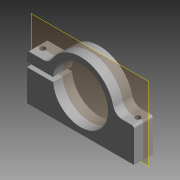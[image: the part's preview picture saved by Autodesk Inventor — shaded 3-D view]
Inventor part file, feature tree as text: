
AUTODESK INVENTOR PART (.ipt)
format: ipt  version: 2013 (Build 170138000, 138)  size: 109,568 bytes
history: native  units: in
note: dims shown in document units (in); Inventor stores cm internally (conversion verified against a paired STEP export)
features: other x3, plane x1
ambient origin geometry x8: Origin, YZ Plane, XZ Plane, XY Plane, X Axis, Y Axis, Z Axis, Center Point
bodies: Solid1 (feature_tree)
feature tree (4):
  other  "Tetrix motor mount.ipt"
  plane  "Work Plane1"
  other  "DC_MOTOR_MOUNT_2011::Tetrix motor mount.ipt"
  other  "TaggingFeature1"
